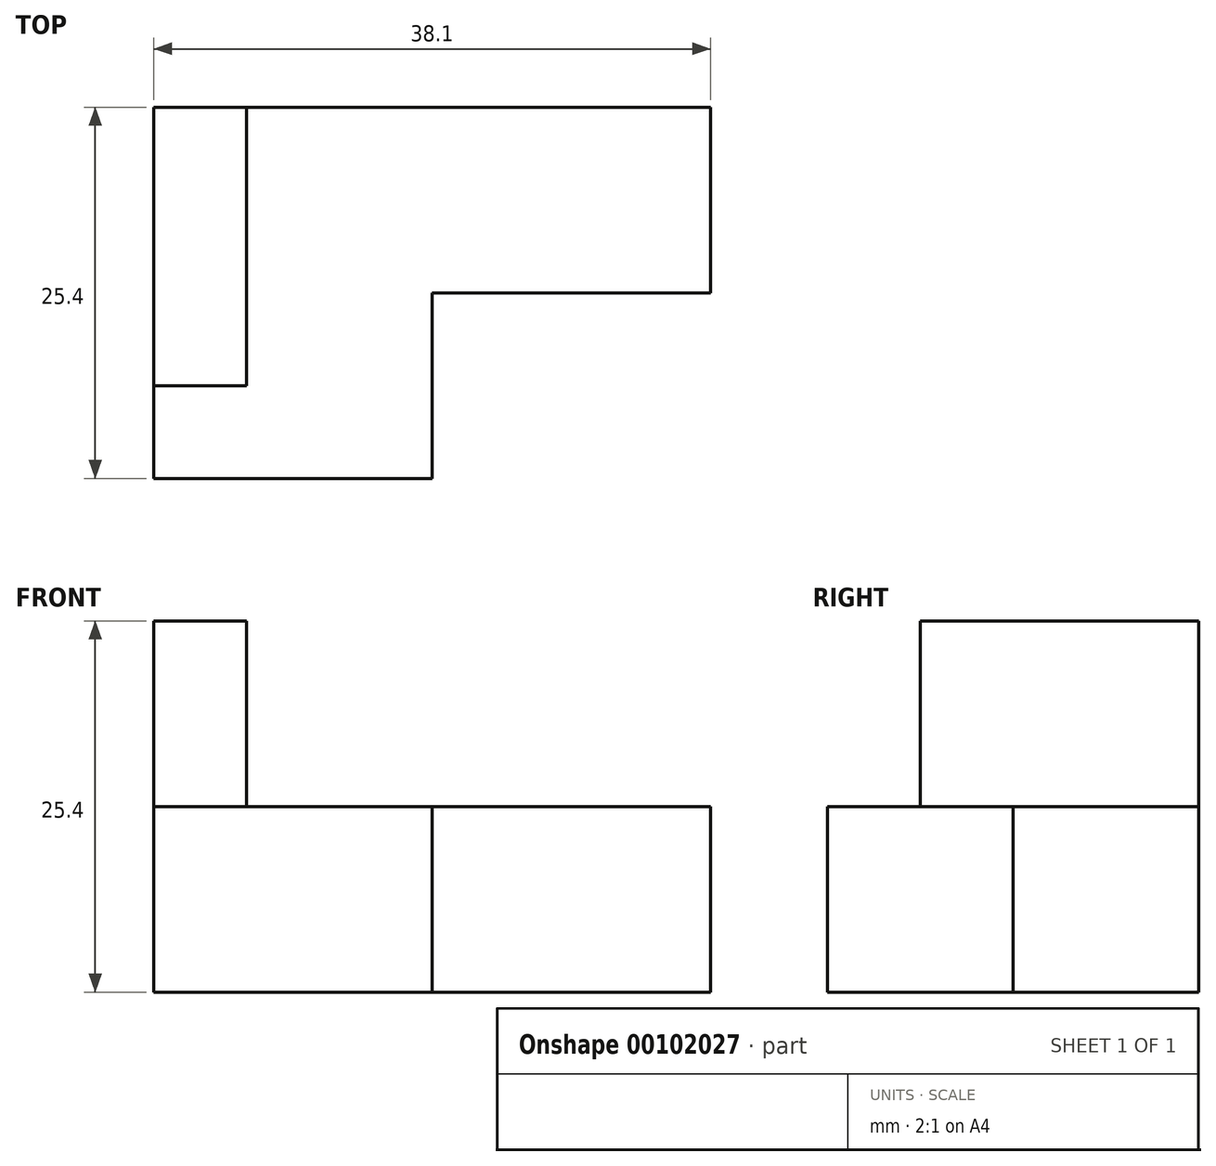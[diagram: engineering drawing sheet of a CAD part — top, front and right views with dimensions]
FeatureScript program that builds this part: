
annotation { "Feature Type Name" : "Feature", "Feature Type Description" : "" }
export const myFeature = defineFeature(function(context is Context, id is Id, definition is map)
    precondition{}
    {
        {
            var Q0;
            Q0=qCreatedBy(makeId("Top.planeOp"),FACE);
            var sketch = newSketch(context, id + "F0", { "sketchPlane" : qUnion([Q0])});
            skLineSegment(sketch, "E0", {"start": v(0, 0) * mm, "end": v(19.05, 0) * mm});
            skLineSegment(sketch, "E1", {"start": v(0, 0) * mm, "end": v(0, 25.4) * mm});
            skLineSegment(sketch, "E2", {"start": v(0, 25.4) * mm, "end": v(38.1, 25.4) * mm});
            skLineSegment(sketch, "E3", {"start": v(38.1, 25.4) * mm, "end": v(38.1, 12.7) * mm});
            skLineSegment(sketch, "E4", {"start": v(38.1, 12.7) * mm, "end": v(19.05, 12.7) * mm});
            skLineSegment(sketch, "E5", {"start": v(19.05, 12.7) * mm, "end": v(19.05, 0) * mm});
            skSolve(sketch);
        }
        {
            var Q0;
            Q0 = qSketchRegion(id + "F0", true);
            extrude(context, id + "F1", {"entities" : qUnion([Q0]), "oppositeDirection" : true, "depth" : 12.7 * mm});
        }
        {
            var Q0;
            Q0=qCreatedBy(makeId("Front.planeOp"),FACE);
            var sketch = newSketch(context, id + "F2", { "sketchPlane" : qUnion([Q0])});
            skLineSegment(sketch, "E6", {"start": v(0, 0) * mm, "end": v(6.35, 0) * mm});
            skLineSegment(sketch, "E7", {"start": v(6.35, 0) * mm, "end": v(6.35, 12.7) * mm});
            skLineSegment(sketch, "E8", {"start": v(6.35, 12.7) * mm, "end": v(0, 12.7) * mm});
            skLineSegment(sketch, "E9", {"start": v(0, 12.7) * mm, "end": v(0, 0) * mm});
            skSolve(sketch);
        }
        {
            var Q0;
            Q0 = qSketchRegion(id + "F2", true);
            extrude(context, id + "F3", {"entities" : qUnion([Q0]), "operationType" : NewBodyOperationType.ADD, "oppositeDirection" : true, "depth" : 25.4 * mm, "hasSecondDirection" : true, "secondDirectionOppositeDirection" : true, "secondDirectionDepth" : 6.35 * mm});
        }
    });
